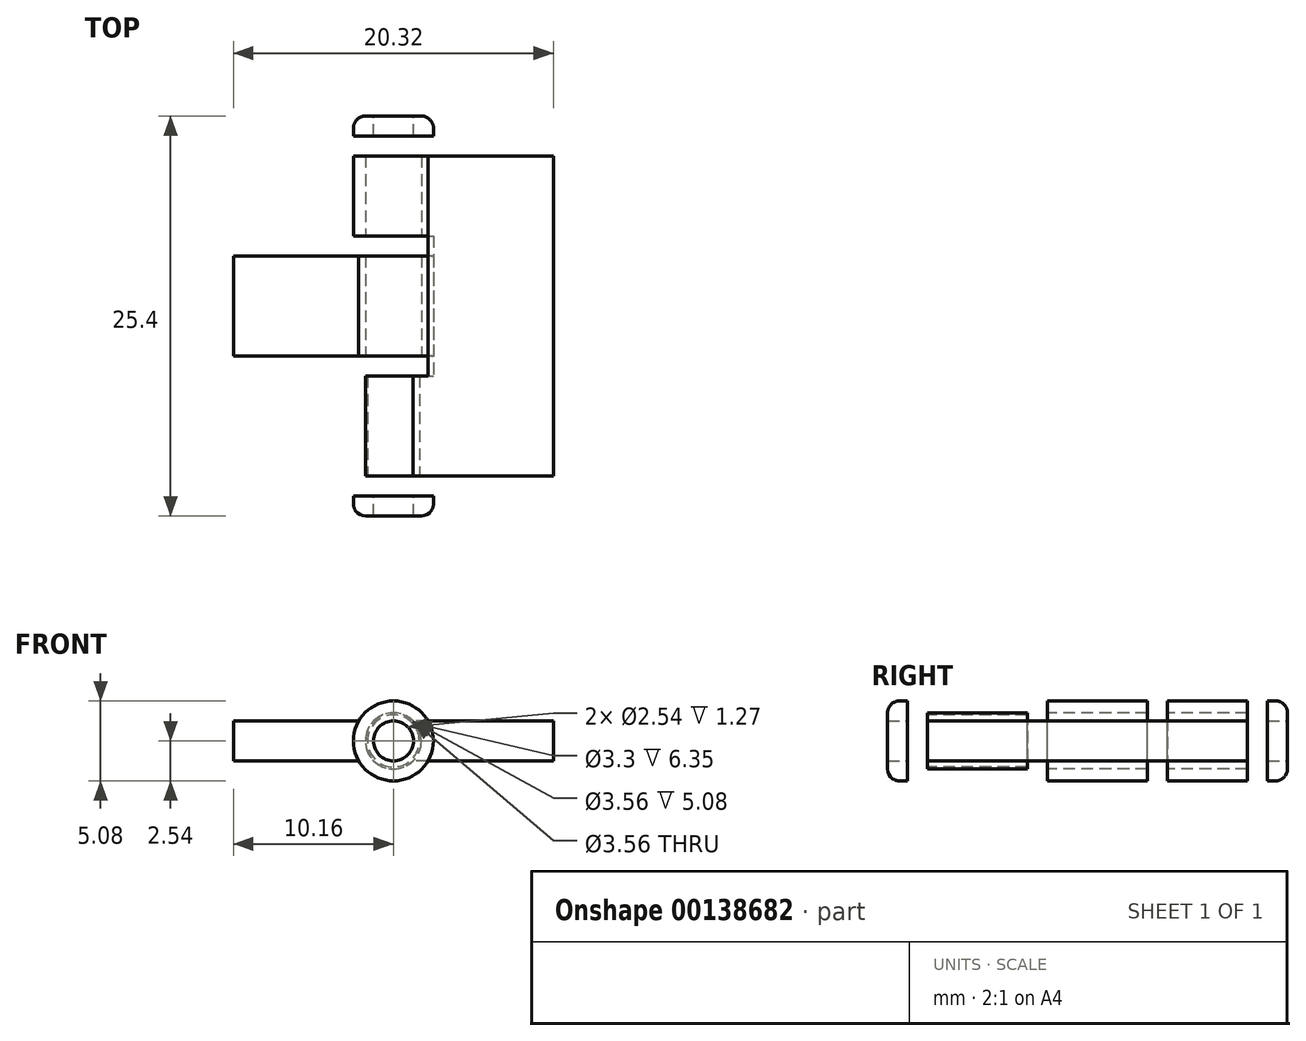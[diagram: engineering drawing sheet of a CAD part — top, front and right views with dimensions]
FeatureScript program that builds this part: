
annotation { "Feature Type Name" : "Feature", "Feature Type Description" : "" }
export const myFeature = defineFeature(function(context is Context, id is Id, definition is map)
    precondition{}
    {
        {
            var Q0;
            Q0=qCreatedBy(makeId("Top.planeOp"),FACE);
            var sketch = newSketch(context, id + "F0", { "sketchPlane" : qUnion([Q0])});
            skLineSegment(sketch, "E0", {"start": v(0, 16.17) * mm, "end": v(0, -18.4) * mm});
            skLineSegment(sketch, "E1.bottom", {"start": v(0, 12.7) * mm, "end": v(1.27, 12.7) * mm});
            skLineSegment(sketch, "E1.top", {"start": v(0, -12.7) * mm, "end": v(1.27, -12.7) * mm});
            skLineSegment(sketch, "E1.left", {"start": v(0, 12.7) * mm, "end": v(0, -12.7) * mm});
            skLineSegment(sketch, "E1.right", {"start": v(1.27, 12.7) * mm, "end": v(1.27, -12.7) * mm});
            skLineSegment(sketch, "E2.bottom", {"start": v(0, 12.7) * mm, "end": v(1.78, 12.7) * mm});
            skLineSegment(sketch, "E2.top", {"start": v(0, 11.43) * mm, "end": v(2.54, 11.43) * mm});
            skLineSegment(sketch, "E2.left", {"start": v(0, 12.7) * mm, "end": v(0, 11.43) * mm});
            skLineSegment(sketch, "E2.right", {"start": v(2.54, 11.94) * mm, "end": v(2.54, 11.43) * mm});
            skLineSegment(sketch, "E3.bottom", {"start": v(0, -12.7) * mm, "end": v(1.78, -12.7) * mm});
            skLineSegment(sketch, "E3.top", {"start": v(0, -11.43) * mm, "end": v(2.54, -11.43) * mm});
            skLineSegment(sketch, "E3.left", {"start": v(0, -12.7) * mm, "end": v(0, -11.43) * mm});
            skLineSegment(sketch, "E3.right", {"start": v(2.54, -11.94) * mm, "end": v(2.54, -11.43) * mm});
            skPoint(sketch, "E4.visualSharp", {"position": v(2.54, 12.7) * mm});
            skArc(sketch, "E4.filletArc", {"start": v(2.54, 11.94) * mm, "mid": v(2.32, 12.48) * mm, "end": v(1.78, 12.7) * mm});
            skPoint(sketch, "E5.visualSharp", {"position": v(2.54, -12.7) * mm});
            skArc(sketch, "E5.filletArc", {"start": v(1.78, -12.7) * mm, "mid": v(2.32, -12.48) * mm, "end": v(2.54, -11.94) * mm});
            skSolve(sketch);
        }
        {
            var Q0;
            {var subQ5=sQuery(id+"F0.wireOp",EDGE,"E2.left");Q0=makeQuery(id+"F0.imprint","IMPRINT",FACE,{"disambiguationData":[TD([[makeQuery(id+"F0.imprint","IMPRINT",EDGE,{"derivedFrom":subQ5}),1.0]])]});}
            var Q1;
            {var subQ0=sQuery(id+"F0.wireOp",EDGE,"E2.right");Q1=makeQuery(id+"F0.imprint","IMPRINT",FACE,{"disambiguationData":[TD([[makeQuery(id+"F0.imprint","IMPRINT",EDGE,{"derivedFrom":subQ0}),-1.0]])]});}
            var Q2;
            {var subQ5=sQuery(id+"F0.wireOp",EDGE,"E3.left");Q2=makeQuery(id+"F0.imprint","IMPRINT",FACE,{"disambiguationData":[TD([[makeQuery(id+"F0.imprint","IMPRINT",EDGE,{"derivedFrom":subQ5}),-1.0]])]});}
            var Q3;
            {var subQ0=sQuery(id+"F0.wireOp",EDGE,"E1.left");Q3=makeQuery(id+"F0.imprint","IMPRINT",FACE,{"disambiguationData":[TD([[makeQuery(id+"F0.imprint","IMPRINT",EDGE,{"derivedFrom":subQ0}),1.0]])]});}
            var Q4;
            {var subQ0=sQuery(id+"F0.wireOp",EDGE,"E3.right");Q4=makeQuery(id+"F0.imprint","IMPRINT",FACE,{"disambiguationData":[TD([[makeQuery(id+"F0.imprint","IMPRINT",EDGE,{"derivedFrom":subQ0}),1.0]])]});}
            var Q5;
            Q5=sQuery(id+"F0.wireOp",EDGE,"E1.left");
            revolve(context, id + "F1", {"entities" : qUnion([Q0, Q1, Q2, Q3, Q4]), "axis" : qUnion([Q5]), "revolveType" : RevolveType.FULL});
        }
        {
            var Q0;
            Q0=qCreatedBy(makeId("Front.planeOp"),FACE);
            cPlane(context, id + "F2", {"entities" : qUnion([Q0]), "cplaneType" : CPlaneType.OFFSET, "offset" : 10.16 * mm, "width" : 152.4 * mm, "height" : 152.4 * mm});
        }
        {
            var Q0;
            Q0=qCreatedBy(id+"F2.planeOp",FACE);
            var sketch = newSketch(context, id + "F3", { "sketchPlane" : qUnion([Q0])});
            skCircle(sketch, "E6.0", {"center": v(0, 0) * mm, "radius": 1.78 * mm});
            skCircle(sketch, "E7.0", {"center": v(0, 0) * mm, "radius": 2.54 * mm});
            skCircle(sketch, "E8", {"center": v(0, 0) * mm, "radius": 1.65 * mm});
            skLineSegment(sketch, "E9.bottom", {"start": v(2.2, -1.27) * mm, "end": v(10.16, -1.27) * mm});
            skLineSegment(sketch, "E9.top", {"start": v(2.2, 1.27) * mm, "end": v(10.16, 1.27) * mm});
            skLineSegment(sketch, "E9.left", {"start": v(2.2, -1.27) * mm, "end": v(2.2, 1.27) * mm});
            skLineSegment(sketch, "E9.right", {"start": v(10.16, -1.27) * mm, "end": v(10.16, 1.27) * mm});
            skLineSegment(sketch, "E10.bottom", {"start": v(3.05, -1.27) * mm, "end": v(1, -1.27) * mm});
            skLineSegment(sketch, "E10.top", {"start": v(3.05, 1.27) * mm, "end": v(1, 1.27) * mm});
            skLineSegment(sketch, "E10.left", {"start": v(3.05, -1.27) * mm, "end": v(3.05, 1.27) * mm});
            skLineSegment(sketch, "E10.right", {"start": v(1, -1.27) * mm, "end": v(1, 1.27) * mm});
            skSolve(sketch);
        }
        {
            var Q0;
            {var subQ0=sQuery(id+"F3.wireOp",EDGE,"E10.bottom");var subQ1=sQuery(id+"F3.wireOp",EDGE,"E6.0");var subQ2=makeQuery(id+"F3.imprint","INTERSECT",VERTEX,{"derivedFrom":[subQ1,subQ0]});Q0=makeQuery(id+"F3.imprint","IMPRINT",FACE,{"disambiguationData":[TD([[makeQuery(id+"F3.imprint","IMPRINT",EDGE,{"disambiguationData":[TD([[subQ2,1.0]])],"derivedFrom":subQ1}),1.0]])]});}
            var Q1;
            {var subQ5=sQuery(id+"F3.wireOp",EDGE,"E9.left");Q1=makeQuery(id+"F3.imprint","IMPRINT",FACE,{"disambiguationData":[TD([[makeQuery(id+"F3.imprint","IMPRINT",EDGE,{"derivedFrom":subQ5}),1.0]])]});}
            var Q2;
            {var subQ0=sQuery(id+"F3.wireOp",EDGE,"E9.left");Q2=makeQuery(id+"F3.imprint","IMPRINT",FACE,{"disambiguationData":[TD([[makeQuery(id+"F3.imprint","IMPRINT",EDGE,{"derivedFrom":subQ0}),-1.0]])]});}
            var Q3;
            {var subQ6=sQuery(id+"F3.wireOp",EDGE,"E10.left");Q3=makeQuery(id+"F3.imprint","IMPRINT",FACE,{"disambiguationData":[TD([[makeQuery(id+"F3.imprint","IMPRINT",EDGE,{"derivedFrom":subQ6}),1.0]])]});}
            var Q4;
            {var subQ0=sQuery(id+"F3.wireOp",EDGE,"E10.bottom");var subQ1=sQuery(id+"F3.wireOp",EDGE,"E6.0");var subQ2=makeQuery(id+"F3.imprint","INTERSECT",VERTEX,{"derivedFrom":[subQ1,subQ0]});Q4=makeQuery(id+"F3.imprint","IMPRINT",FACE,{"disambiguationData":[TD([[makeQuery(id+"F3.imprint","IMPRINT",EDGE,{"disambiguationData":[TD([[subQ2,-1.0]])],"derivedFrom":subQ1}),1.0]])]});}
            extrude(context, id + "F4", {"entities" : qUnion([Q0, Q1, Q2, Q3, Q4]), "oppositeDirection" : true, "depth" : 6.35 * mm});
        }
        {
            var Q0;
            Q0=makeQuery(id+"F3.imprint","IMPRINT",FACE,{"disambiguationData":[TD([[makeQuery(id+"F3.imprint","IMPRINT",EDGE,{"derivedFrom":sQuery(id+"F3.wireOp",EDGE,"E9.bottom")}),1.0]])]});
            extrude(context, id + "F5", {"entities" : qUnion([Q0]), "operationType" : NewBodyOperationType.ADD, "oppositeDirection" : true, "depth" : 20.32 * mm});
        }
        {
            var Q0;
            Q0=qCreatedBy(id+"F2.planeOp",FACE);
            cPlane(context, id + "F6", {"entities" : qUnion([Q0]), "cplaneType" : CPlaneType.OFFSET, "offset" : 15.24 * mm, "oppositeDirection" : true, "width" : 152.4 * mm, "height" : 152.4 * mm});
        }
        {
            var Q0;
            Q0=qCreatedBy(id+"F6.planeOp",FACE);
            var sketch = newSketch(context, id + "F7", { "sketchPlane" : qUnion([Q0])});
            skCircle(sketch, "E11.0", {"center": v(0, 0) * mm, "radius": 2.54 * mm});
            skCircle(sketch, "E12.0", {"center": v(0, 0) * mm, "radius": 1.78 * mm});
            skCircle(sketch, "E13.0", {"center": v(0, 0) * mm, "radius": 1.65 * mm});
            skPoint(sketch, "E14.0", {"position": v(2.2, 1.27) * mm});
            skLineSegment(sketch, "E15.0", {"start": v(3.05, 1.27) * mm, "end": v(1, 1.27) * mm});
            skLineSegment(sketch, "E16.0", {"start": v(3.05, -1.27) * mm, "end": v(1, -1.27) * mm});
            skPoint(sketch, "E17.0", {"position": v(3.05, 0) * mm});
            skLineSegment(sketch, "E18.0", {"start": v(3.05, -1.27) * mm, "end": v(3.05, 1.27) * mm});
            skSolve(sketch);
        }
        {
            var Q0;
            Q0=makeQuery(id+"F7.imprint","IMPRINT",FACE,{"disambiguationData":[TD([[makeQuery(id+"F7.imprint","IMPRINT",EDGE,{"derivedFrom":sQuery(id+"F7.wireOp",EDGE,"E11.0")}),1.0]])]});
            var Q1;
            {var subQ5=sQuery(id+"F7.wireOp",EDGE,"E18.0");Q1=makeQuery(id+"F7.imprint","IMPRINT",FACE,{"disambiguationData":[TD([[makeQuery(id+"F7.imprint","IMPRINT",EDGE,{"derivedFrom":subQ5}),1.0]])]});}
            extrude(context, id + "F8", {"entities" : qUnion([Q0, Q1]), "operationType" : NewBodyOperationType.ADD, "oppositeDirection" : true, "depth" : 5.08 * mm});
        }
        {
            var Q0;
            Q0=qCreatedBy(id+"F6.planeOp",FACE);
            cPlane(context, id + "F9", {"entities" : qUnion([Q0]), "cplaneType" : CPlaneType.OFFSET, "offset" : 7.62 * mm, "width" : 152.4 * mm, "height" : 152.4 * mm});
        }
        {
            var Q0;
            Q0=qCreatedBy(id+"F9.planeOp",FACE);
            var sketch = newSketch(context, id + "F10", { "sketchPlane" : qUnion([Q0])});
            skCircle(sketch, "E19.0", {"center": v(0, 0) * mm, "radius": 2.54 * mm});
            skCircle(sketch, "E20.0", {"center": v(0, 0) * mm, "radius": 1.78 * mm});
            skLineSegment(sketch, "E21.0", {"start": v(2.2, 1.27) * mm, "end": v(10.16, 1.27) * mm});
            skPoint(sketch, "E22.0", {"position": v(6.18, 1.27) * mm});
            skLineSegment(sketch, "E23.bottom", {"start": v(-2.2, -1.27) * mm, "end": v(-10.16, -1.27) * mm});
            skLineSegment(sketch, "E23.top", {"start": v(-2.2, 1.27) * mm, "end": v(-10.16, 1.27) * mm});
            skLineSegment(sketch, "E23.left", {"start": v(-2.2, -1.27) * mm, "end": v(-2.2, 1.27) * mm});
            skLineSegment(sketch, "E23.right", {"start": v(-10.16, -1.27) * mm, "end": v(-10.16, 1.27) * mm});
            skSolve(sketch);
        }
        {
            var Q0;
            Q0=makeQuery(id+"F10.imprint","IMPRINT",FACE,{"disambiguationData":[TD([[makeQuery(id+"F10.imprint","IMPRINT",EDGE,{"derivedFrom":sQuery(id+"F10.wireOp",EDGE,"E19.0")}),1.0]])]});
            var Q1;
            {var subQ0=sQuery(id+"F10.wireOp",EDGE,"E23.left");Q1=makeQuery(id+"F10.imprint","IMPRINT",FACE,{"disambiguationData":[TD([[makeQuery(id+"F10.imprint","IMPRINT",EDGE,{"derivedFrom":subQ0}),1.0]])]});}
            var Q2;
            {var subQ1=sQuery(id+"F10.wireOp",EDGE,"E23.bottom");Q2=makeQuery(id+"F10.imprint","IMPRINT",FACE,{"disambiguationData":[TD([[makeQuery(id+"F10.imprint","IMPRINT",EDGE,{"derivedFrom":subQ1}),-1.0]])]});}
            extrude(context, id + "F11", {"entities" : qUnion([Q0, Q1, Q2]), "oppositeDirection" : true, "depth" : 6.35 * mm});
        }
    });
